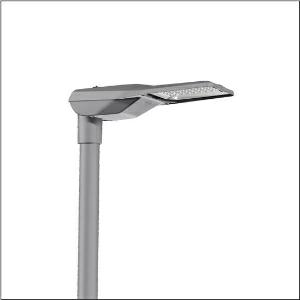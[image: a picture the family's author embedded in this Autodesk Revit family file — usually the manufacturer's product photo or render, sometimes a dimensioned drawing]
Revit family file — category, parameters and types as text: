
# Revit family: streetlight_sl_21_mini___st1_0a_5xe2d43s08gb_5b06
name_source: partatom
category: Lighting Fixtures
units: mm (PartAtom-declared; Revit-internal decimal feet)

## family parameters
Cut with Voids When Loaded = No
Host = Face
Light Source = No
Part Type = Normal
Room Calculation Point = No
Round Connector Dimension = Use Diameter
Shared = No

## types (1)
- --- (1 x LED, 6180 lm, 40.4 W, 4000K)
    Apparent Load = 40 VA
    CIE Flux Codes = 37 72 97 100 100
    Color Rendering = 70
    Color Temperature = 4000K
    Default Elevation = 1800 mm
    Description = Streetlight SL 21 mini, mast luminaire, primary light control with lens, of PMMA, primary optical cover: cover, of toughened safety glass, transparent, light distribution: ST1.0a, light emission: direct distribution, primary light characteristic: asymmetric, installation type: side-entry, post-top, LED, High Power LED, rated luminous flux: 6.180lm, luminous efficacy: 153lm/W, light colour: 740, colour temperature: 4000K, control gear: D4i, control: overheat protection, constant luminous flux control, time-dependent luminous flux control, flexible luminous flux parameterisation, pre-setting: logarithmic dimming characteristic, mains connection: 220..240V, AC, 50/60Hz, start of lifetime: 40W, end of service life: 41W, reduction: 19W, luminaire housing, of diecast aluminium, powder-coated, Siteco® metallic grey (DB 702S), corrosivity category C5 high according to DIN EN ISO 12944, please order mast flange separately, inclination adjustable: 0°, 5°, 10°, 15°, sealing non-destructively replaceable, multi-level sealing system, length: 628mm, width: 235mm, height: 110mm, mast flange for spigot size: 42mm (side-entry): 5XC10008XM4, 60/48mm (side-entry/post-top): 5XC10108XM2, 76/60mm (side-entry/post-top): 5XC10108XM1, mounting height: 4..8m, Smart Interface above, protection rating (complete): IP66, insulation class (complete): insulation class II (safety insulation), certification: CE, ENEC, ENEC+, VDE, impact resistance: IK10, permissible operating ambient temperature for outdoor applications: -40..+50°C, standard-compliant lighting for roads and squares, packaging unit: 1 piece

Light Distribution: ST1.0a
    Height = 110 mm
    Lamp = 1 x LED
    Lamp Light Flux = 6180 lm
    Lamp Power = 40.4 W
    Lamp count = 1
    Length = 625 mm
    Luminous efficacy = 153 lm/W
    Manufacturer = Siteco
    ModVariant = No
    Model = 5XE2D43S08GB
    Number of Poles = 1
    OnlyDefault = Yes
    Power Factor = 1
    Product Name = Streetlight SL 21 mini | ST1.0a
    Product group = mast luminaire | pylon top
    ProductGroupID = 6100
    Protection Class = Protection class II
    Protection Degree = IP 66
    RLX_Detail_Level = 1
    RLX_Emergency_Light_Flux = 0 lm
    RLX_Emergency_Type = 0
    RLX_Emergency_Type_DB = No
    RlxData = <blob elided: 26101 chars, md5=8a578d7b>
    Socket = socket
    Standby Power = 0 W
    System Light Flux = 6180 lm
    System Power = 40 W
    Type Comments = factory setting: luminous flux: 100 % | dim-lin: 254 | 812 mA
    Type Image = l_1003515.jpg
    URL = http://relux.com
    VarID = @adj_189937
    Voltage = 0 V
    Weight = 0.00 kg
    Width = 234 mm

## geometry (parser evidence)
native form markers: Blend x4, Sweep x10
no freeform markers — native parametric forms only
